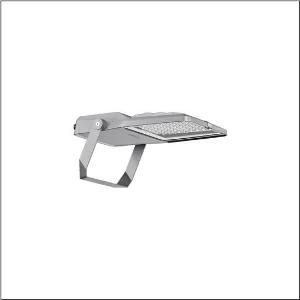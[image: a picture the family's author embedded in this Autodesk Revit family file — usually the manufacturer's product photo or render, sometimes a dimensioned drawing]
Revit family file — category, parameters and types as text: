
# Revit family: floodlight_fl_21_iq_mini___rs12_5xa7772d4b1a_8fae
name_source: partatom
category: Lighting Fixtures
units: mm (PartAtom-declared; Revit-internal decimal feet)

## family parameters
Cut with Voids When Loaded = No
Host = Face
Light Source = No
Part Type = Normal
Room Calculation Point = No
Round Connector Dimension = Use Diameter
Shared = No

## types (1)
- --- (1 x LED, 18810 lm, 143 W, 4000K)
    Apparent Load = 143 VA
    CIE Flux Codes = 79 92 99 100 100
    Color Rendering = 70
    Color Temperature = 4000K
    Default Elevation = 1800 mm
    Description = Floodlight FL 21 iQ mini, floodlight, primary light control with lens, of PMMA, primary optical cover: protective disc, of toughened safety glass, transparent, light distribution: RS12, light emission: direct distribution, installation type: surface-mounted, LED, High Power LED, rated luminous flux: 18.810lm, luminous efficacy: 132lm/W, light colour: 740, colour temperature: 4000K, control: Street-Remote, Auto-Match, Temp-Guard, Night-Set, Smart-Wire, Desk-Remote (wireless, voltage-free reading and setting of iQ features in the workshop via application-optimized NFC function/RFID function), optimised constant luminous flux control (CLO 2.0), with terminal, 6-pole, mains connection: 220..240V, AC, 50/60Hz, start of lifetime: 143W, end of service life: 152W, reduction: 61W, luminaire housing, of diecast aluminium, powder-coated, Siteco® metallic grey (DB 702S), corrosivity category C5 mid according to DIN EN ISO 12944, sealing non-destructively replaceable, mounting bracket, of steel, galvanised, powder-coated, Siteco® metallic grey (DB 702S), protection rating (complete): IP66, insulation class (complete): insulation class II (safety insulation), certification: CE, ENEC, VDE, protection symbol: D, impact resistance: IK08, permissible operating ambient temperature: -40..+40°C, permissible operating ambient temperature for outdoor applications: -40..+50°C, standard: DIN EN 12944, LABS conformity tested according to VDMA 24364:2018-05, packaging unit: 1 piece

Light Distribution: RS12
    Height = 70 mm
    Lamp = 1 x LED
    Lamp Light Flux = 18810 lm
    Lamp Power = 143 W
    Lamp count = 1
    Length = 485 mm
    Luminous efficacy = 132 lm/W
    Manufacturer = Siteco
    ModVariant = No
    Model = 5XA7772D4B1A
    Number of Poles = 1
    OnlyDefault = Yes
    Power Factor = 1
    Product Name = Floodlight FL 21 iQ mini | RS12
    Product group = floodlight | pylon annexe
    ProductGroupID = 6200
    Protection Class = Protection class II
    Protection Degree = IP 66
    RLX_Detail_Level = 1
    RLX_Emergency_Light_Flux = 0 lm
    RLX_Emergency_Type = 0
    RLX_Emergency_Type_DB = No
    RlxData = <blob elided: 91253 chars, md5=f77c7162>
    Socket = socket
    Standby Power = 0 W
    System Light Flux = 18810 lm
    System Power = 143 W
    Type Comments = factory setting: luminous flux: 100 % | dim-lin: 254 | 730 mA
    Type Image = l_1006845.jpg
    URL = http://relux.com
    VarID = @adj_099615
    Voltage = 0 V
    Weight = 0.00 kg
    Width = 337 mm

## geometry (parser evidence)
native form markers: Blend x4, Sweep x13
no freeform markers — native parametric forms only
